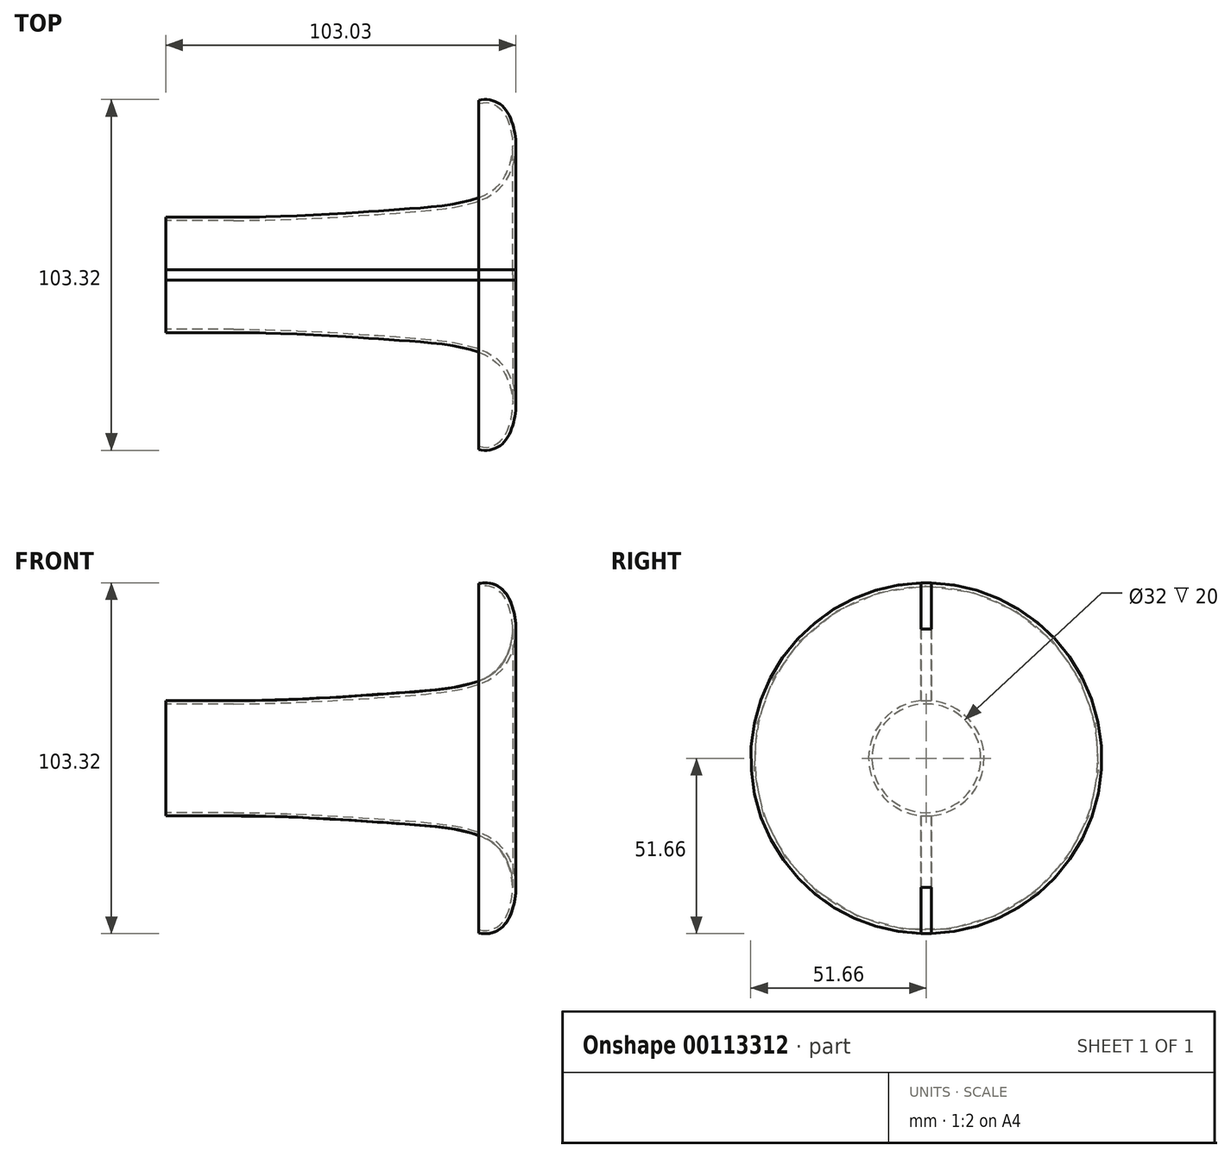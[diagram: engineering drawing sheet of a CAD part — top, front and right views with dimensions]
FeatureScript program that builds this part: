
annotation { "Feature Type Name" : "Feature", "Feature Type Description" : "" }
export const myFeature = defineFeature(function(context is Context, id is Id, definition is map)
    precondition{}
    {
        {
            var Q0;
            Q0=qCreatedBy(makeId("Front.planeOp"),FACE);
            var sketch = newSketch(context, id + "F0", { "sketchPlane" : qUnion([Q0])});
            skLineSegment(sketch, "E0", {"start": v(0, -16) * mm, "end": v(20, -16) * mm});
            skPoint(sketch, "E1", {"position": v(94.68, -22.86) * mm});
            skPoint(sketch, "E2", {"position": v(101.72, -30.9) * mm});
            skPoint(sketch, "E3", {"position": v(104.69, -47.78) * mm});
            skPoint(sketch, "E4", {"position": v(92.03, -51.46) * mm});
            skFitSpline(sketch, "E5", {"points": [v(20, -16) * mm, v(67.06, -18.16) * mm, v(94.68, -22.86) * mm, v(101.72, -30.9) * mm, v(102.46, -42.9) * mm, v(92.03, -51.46) * mm], "startDerivative": vector(160.9, -0.68) * mm, "endDerivative": vector(-121.87, 23.41) * mm});
            skFitSpline(sketch, "E6.0", {"points": [v(20, -17) * mm, v(23.34, -17.01) * mm, v(30.02, -17.13) * mm, v(39.92, -17.49) * mm, v(49.64, -18) * mm, v(57.53, -18.5) * mm, v(63.68, -18.92) * mm, v(68.21, -19.24) * mm, v(72.62, -19.56) * mm, v(78.28, -20.05) * mm, v(83.5, -20.67) * mm, v(88.07, -21.58) * mm, v(91.13, -22.41) * mm, v(93.75, -23.44) * mm, v(95.89, -24.67) * mm, v(97.6, -26.1) * mm, v(98.98, -27.72) * mm, v(99.89, -29.22) * mm, v(100.5, -30.5) * mm, v(101.03, -31.85) * mm, v(101.56, -33.6) * mm, v(101.96, -35.84) * mm, v(102.08, -38.19) * mm, v(101.94, -40.24) * mm, v(101.66, -41.92) * mm, v(101.37, -43.22) * mm, v(100.99, -44.52) * mm, v(100.35, -46.2) * mm, v(99.5, -47.71) * mm, v(98.44, -48.94) * mm, v(97.52, -49.68) * mm, v(96.48, -50.24) * mm, v(94.88, -50.7) * mm, v(93.38, -50.7) * mm, v(92.22, -50.48) * mm]});
            skLineSegment(sketch, "E6.1", {"start": v(0, -17) * mm, "end": v(20, -17) * mm});
            skLineSegment(sketch, "E7", {"start": v(0, -17) * mm, "end": v(0, -16) * mm});
            skLineSegment(sketch, "E8", {"start": v(92.03, -51.46) * mm, "end": v(92.22, -50.48) * mm});
            skLineSegment(sketch, "E9", {"start": v(0, 0) * mm, "end": v(153.3, 0) * mm, "construction": true});
            skLineSegment(sketch, "E10", {"start": v(92.03, -51.46) * mm, "end": v(87.03, -51.46) * mm});
            skLineSegment(sketch, "E11", {"start": v(77.03, -41.46) * mm, "end": v(77.03, -19.96) * mm});
            skPoint(sketch, "E12.visualSharp", {"position": v(77.03, -51.46) * mm});
            skArc(sketch, "E12.filletArc", {"start": v(77.03, -41.46) * mm, "mid": v(79.96, -48.53) * mm, "end": v(87.03, -51.46) * mm});
            skCircle(sketch, "E13", {"center": v(87.03, -41.46) * mm, "radius": 3 * mm});
            skSolve(sketch);
        }
        {
            var Q0;
            Q0=makeQuery(id+"F0.imprint","IMPRINT",FACE,{"disambiguationData":[TD([[makeQuery(id+"F0.imprint","IMPRINT",EDGE,{"derivedFrom":sQuery(id+"F0.wireOp",EDGE,"E0")}),-1.0]])]});
            var Q1;
            Q1=sQuery(id+"F0.wireOp",EDGE,"E9");
            revolve(context, id + "F1", {"entities" : qUnion([Q0]), "axis" : qUnion([Q1]), "revolveType" : RevolveType.FULL});
        }
        {
            var Q0;
            Q0=makeQuery(id+"F0.imprint","IMPRINT",FACE,{"disambiguationData":[TD([[makeQuery(id+"F0.imprint","IMPRINT",EDGE,{"derivedFrom":sQuery(id+"F0.wireOp",EDGE,"E0")}),-1.0]])]});
            var Q1;
            {var subQ1=sQuery(id+"F0.wireOp",EDGE,"E8");Q1=makeQuery(id+"F0.imprint","IMPRINT",FACE,{"disambiguationData":[TD([[makeQuery(id+"F0.imprint","IMPRINT",EDGE,{"derivedFrom":subQ1}),1.0]])]});}
            extrude(context, id + "F2", {"entities" : qUnion([Q0, Q1]), "operationType" : NewBodyOperationType.ADD, "endBound" : BoundingType.SYMMETRIC, "depth" : 3 * mm});
        }
        {
            var Q0;
            Q0=makeQuery(id+"F1.opRevolve","SWEPT_BODY",BODY,{"disambiguationData":[OSD([sQuery(id+"F0.wireOp",EDGE,"E0"),sQuery(id+"F0.wireOp",EDGE,"E5"),sQuery(id+"F0.wireOp",EDGE,"E6.0"),sQuery(id+"F0.wireOp",EDGE,"E6.1"),sQuery(id+"F0.wireOp",EDGE,"E7"),sQuery(id+"F0.wireOp",EDGE,"E8")])]});
            var Q1;
            Q1=qCreatedBy(makeId("Top.planeOp"),FACE);
            mirror(context, id + "F3", {"operationType" : NewBodyOperationType.ADD, "entities" : qUnion([Q0]), "mirrorPlane" : qUnion([Q1])});
        }
    });
